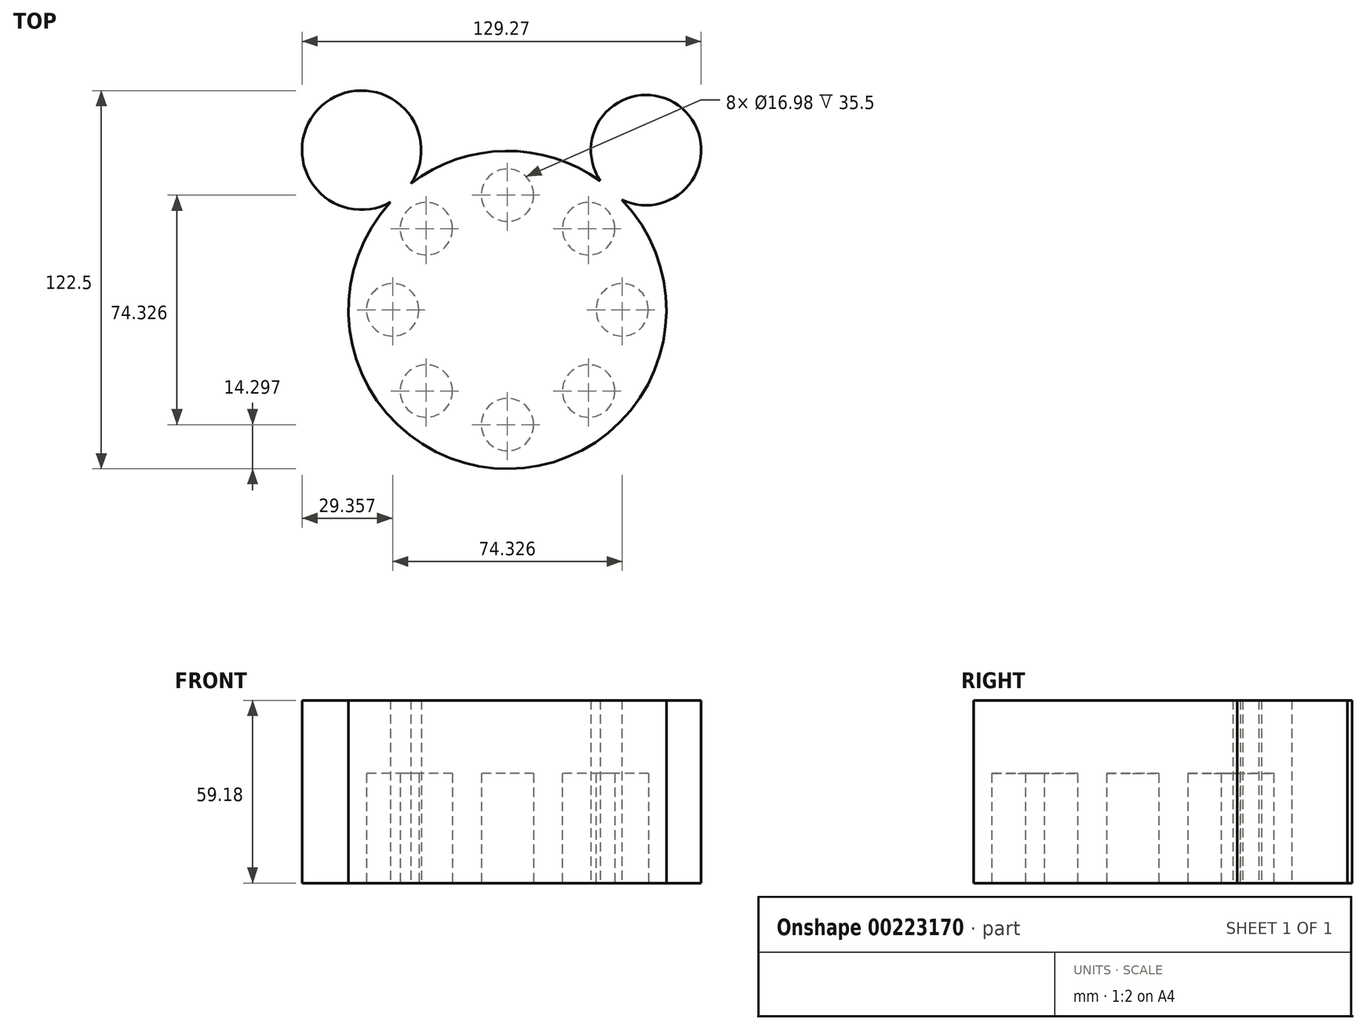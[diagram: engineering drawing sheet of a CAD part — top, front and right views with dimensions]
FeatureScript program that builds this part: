
annotation { "Feature Type Name" : "Feature", "Feature Type Description" : "" }
export const myFeature = defineFeature(function(context is Context, id is Id, definition is map)
    precondition{}
    {
        {
            var Q0;
            Q0=qCreatedBy(makeId("Top.planeOp"),FACE);
            var sketch = newSketch(context, id + "F0", { "sketchPlane" : qUnion([Q0])});
            skCircle(sketch, "E0", {"center": v(0, 0) * mm, "radius": 51.46 * mm});
            skSolve(sketch);
        }
        {
            var Q0;
            Q0 = qSketchRegion(id + "F0", true);
            extrude(context, id + "F1", {"entities" : qUnion([Q0]), "depth" : 25.4 * mm});
        }
        {
            var Q0;
            Q0=makeQuery(id+"F1.opExtrude","CAP_FACE",FACE,{"disambiguationData":[OSD([sQuery(id+"F0.wireOp",EDGE,"E0")])],"isStart":false});
            extrude(context, id + "F2", {"entities" : qUnion([Q0]), "operationType" : NewBodyOperationType.ADD, "depth" : 28.96 * mm});
        }
        {
            var Q0;
            Q0=qCreatedBy(makeId("Top.planeOp"),FACE);
            var sketch = newSketch(context, id + "F3", { "sketchPlane" : qUnion([Q0])});
            skCircle(sketch, "E1", {"center": v(-47.22, 51.74) * mm, "radius": 19.3 * mm});
            skCircle(sketch, "E2", {"center": v(44.89, 51.74) * mm, "radius": 17.86 * mm});
            skSolve(sketch);
        }
        {
            var Q0;
            Q0=makeQuery(id+"F3.imprint","IMPRINT",FACE,{"disambiguationData":[TD([[makeQuery(id+"F3.imprint","IMPRINT",EDGE,{"derivedFrom":sQuery(id+"F3.wireOp",EDGE,"E2")}),1.0]])]});
            var Q1;
            Q1=makeQuery(id+"F1.opExtrude","CAP_FACE",FACE,{"disambiguationData":[OSD([sQuery(id+"F0.wireOp",EDGE,"E0")])],"isStart":true});
            var Q2;
            Q2=makeQuery(id+"F3.imprint","IMPRINT",FACE,{"disambiguationData":[TD([[makeQuery(id+"F3.imprint","IMPRINT",EDGE,{"derivedFrom":sQuery(id+"F3.wireOp",EDGE,"E1")}),1.0]])]});
            extrude(context, id + "F4", {"entities" : qUnion([Q0, Q1, Q2]), "operationType" : NewBodyOperationType.ADD, "depth" : 59.18 * mm});
        }
        {
            var Q0;
            Q0=qCreatedBy(makeId("Top.planeOp"),FACE);
            var sketch = newSketch(context, id + "F5", { "sketchPlane" : qUnion([Q0])});
            skCircle(sketch, "E3", {"center": v(0, 37.16) * mm, "radius": 8.49 * mm});
            skCircle(sketch, "E4.1.0", {"center": v(-26.28, 26.28) * mm, "radius": 8.49 * mm});
            skCircle(sketch, "E4.2.0", {"center": v(-37.16, 0) * mm, "radius": 8.49 * mm});
            skCircle(sketch, "E4.3.0", {"center": v(-26.28, -26.28) * mm, "radius": 8.49 * mm});
            skCircle(sketch, "E4.4.0", {"center": v(0, -37.16) * mm, "radius": 8.49 * mm});
            skCircle(sketch, "E4.5.0", {"center": v(26.28, -26.28) * mm, "radius": 8.49 * mm});
            skCircle(sketch, "E4.6.0", {"center": v(37.16, 0) * mm, "radius": 8.49 * mm});
            skCircle(sketch, "E4.7.0", {"center": v(26.28, 26.28) * mm, "radius": 8.49 * mm});
            skPoint(sketch, "E4.center", {"position": v(0, 0) * mm});
            skSolve(sketch);
        }
        {
            var Q0;
            Q0=makeQuery(id+"F5.imprint","IMPRINT",FACE,{"disambiguationData":[TD([[makeQuery(id+"F5.imprint","IMPRINT",EDGE,{"derivedFrom":sQuery(id+"F5.wireOp",EDGE,"E4.2.0")}),1.0]])]});
            var Q1;
            Q1=makeQuery(id+"F5.imprint","IMPRINT",FACE,{"disambiguationData":[TD([[makeQuery(id+"F5.imprint","IMPRINT",EDGE,{"derivedFrom":sQuery(id+"F5.wireOp",EDGE,"E4.1.0")}),1.0]])]});
            var Q2;
            Q2=makeQuery(id+"F5.imprint","IMPRINT",FACE,{"disambiguationData":[TD([[makeQuery(id+"F5.imprint","IMPRINT",EDGE,{"derivedFrom":sQuery(id+"F5.wireOp",EDGE,"E3")}),1.0]])]});
            var Q3;
            Q3=makeQuery(id+"F5.imprint","IMPRINT",FACE,{"disambiguationData":[TD([[makeQuery(id+"F5.imprint","IMPRINT",EDGE,{"derivedFrom":sQuery(id+"F5.wireOp",EDGE,"E4.7.0")}),1.0]])]});
            var Q4;
            Q4=makeQuery(id+"F5.imprint","IMPRINT",FACE,{"disambiguationData":[TD([[makeQuery(id+"F5.imprint","IMPRINT",EDGE,{"derivedFrom":sQuery(id+"F5.wireOp",EDGE,"E4.6.0")}),1.0]])]});
            var Q5;
            Q5=makeQuery(id+"F5.imprint","IMPRINT",FACE,{"disambiguationData":[TD([[makeQuery(id+"F5.imprint","IMPRINT",EDGE,{"derivedFrom":sQuery(id+"F5.wireOp",EDGE,"E4.5.0")}),1.0]])]});
            var Q6;
            Q6=makeQuery(id+"F5.imprint","IMPRINT",FACE,{"disambiguationData":[TD([[makeQuery(id+"F5.imprint","IMPRINT",EDGE,{"derivedFrom":sQuery(id+"F5.wireOp",EDGE,"E4.4.0")}),1.0]])]});
            var Q7;
            Q7=makeQuery(id+"F5.imprint","IMPRINT",FACE,{"disambiguationData":[TD([[makeQuery(id+"F5.imprint","IMPRINT",EDGE,{"derivedFrom":sQuery(id+"F5.wireOp",EDGE,"E4.3.0")}),1.0]])]});
            extrude(context, id + "F6", {"entities" : qUnion([Q0, Q1, Q2, Q3, Q4, Q5, Q6, Q7]), "operationType" : NewBodyOperationType.REMOVE, "depth" : 35.5 * mm});
        }
    });
